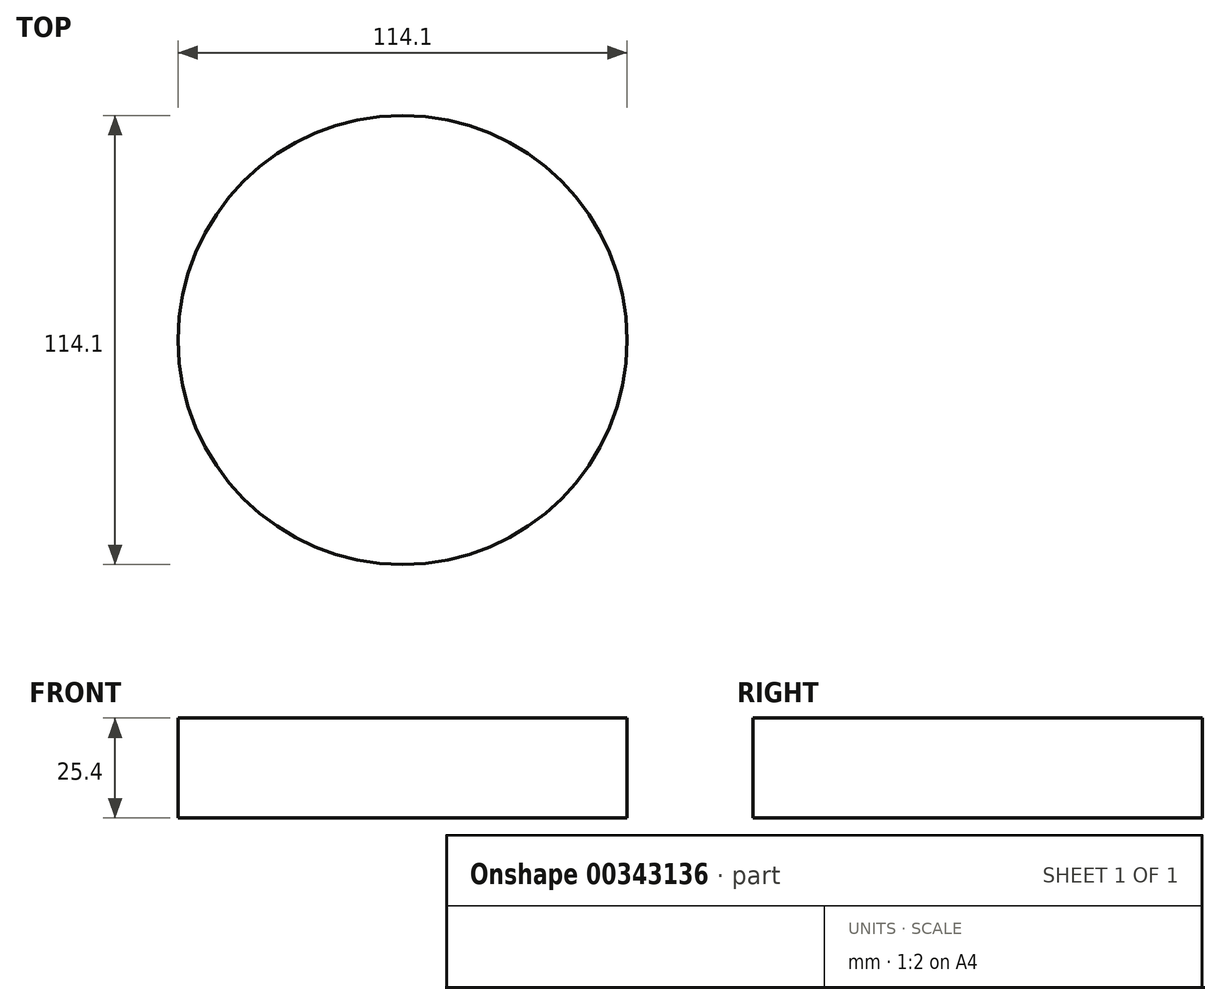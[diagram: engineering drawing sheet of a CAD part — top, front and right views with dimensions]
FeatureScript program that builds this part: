
annotation { "Feature Type Name" : "Feature", "Feature Type Description" : "" }
export const myFeature = defineFeature(function(context is Context, id is Id, definition is map)
    precondition{}
    {
        {
            var Q0;
            Q0=qCreatedBy(makeId("Top.planeOp"),FACE);
            var sketch = newSketch(context, id + "F0", { "sketchPlane" : qUnion([Q0])});
            skCircle(sketch, "E0", {"center": v(0, 1.34) * mm, "radius": 57.05 * mm});
            skSolve(sketch);
        }
        {
            var Q0;
            Q0=makeQuery(id+"F0.imprint","IMPRINT",FACE,{"disambiguationData":[TD([[makeQuery(id+"F0.imprint","IMPRINT",EDGE,{"derivedFrom":sQuery(id+"F0.wireOp",EDGE,"E0")}),1.0]])]});
            extrude(context, id + "F1", {"entities" : qUnion([Q0]), "depth" : 25.4 * mm});
        }
    });
